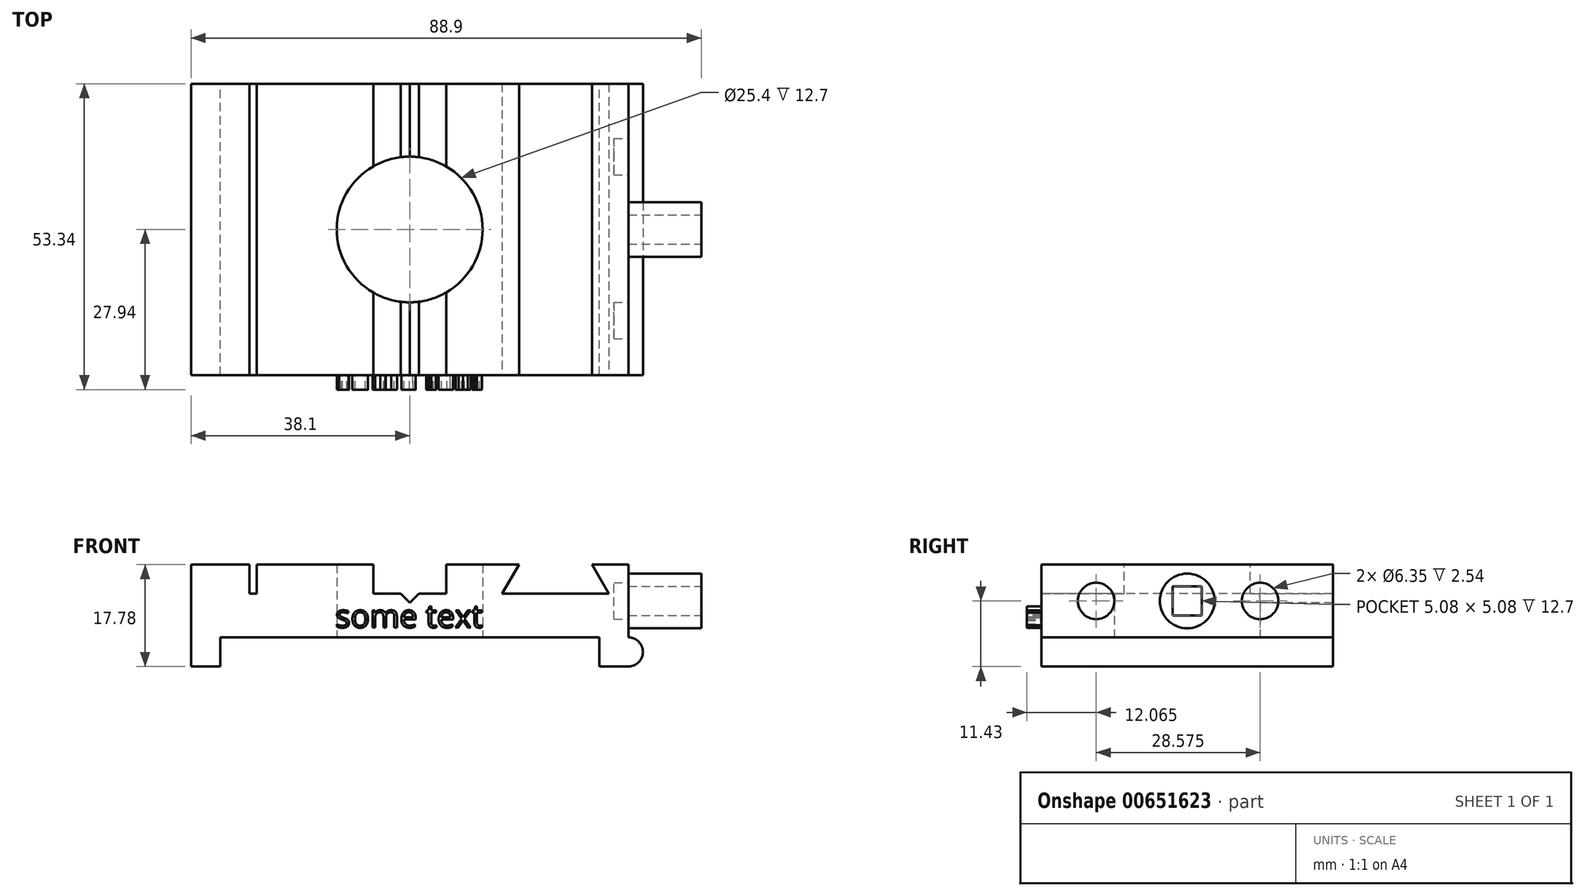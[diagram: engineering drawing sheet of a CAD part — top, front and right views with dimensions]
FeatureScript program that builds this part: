
annotation { "Feature Type Name" : "Feature", "Feature Type Description" : "" }
export const myFeature = defineFeature(function(context is Context, id is Id, definition is map)
    precondition{}
    {
        {
            var Q0;
            Q0=qCreatedBy(makeId("Top.planeOp"),FACE);
            var sketch = newSketch(context, id + "F0", { "sketchPlane" : qUnion([Q0])});
            skLineSegment(sketch, "E0.bottom", {"start": v(38.1, 25.4) * mm, "end": v(-38.1, 25.4) * mm});
            skLineSegment(sketch, "E0.top", {"start": v(38.1, -25.4) * mm, "end": v(-38.1, -25.4) * mm});
            skLineSegment(sketch, "E0.left", {"start": v(38.1, 25.4) * mm, "end": v(38.1, -25.4) * mm});
            skLineSegment(sketch, "E0.right", {"start": v(-38.1, 25.4) * mm, "end": v(-38.1, -25.4) * mm});
            skPoint(sketch, "E0.middle", {"position": v(0, 0) * mm});
            skCircle(sketch, "E1", {"center": v(0, 0) * mm, "radius": 12.7 * mm});
            skSolve(sketch);
        }
        {
            var Q0;
            Q0=makeQuery(id+"F0.imprint","IMPRINT",FACE,{"disambiguationData":[TD([[makeQuery(id+"F0.imprint","IMPRINT",EDGE,{"derivedFrom":sQuery(id+"F0.wireOp",EDGE,"E0.bottom")}),1.0]])]});
            extrude(context, id + "F1", {"entities" : qUnion([Q0]), "depth" : 12.7 * mm});
        }
        {
            var Q0;
            Q0=makeQuery(id+"F1.opExtrude","CAP_FACE",FACE,{"disambiguationData":[OSD([sQuery(id+"F0.wireOp",EDGE,"E0.bottom"),sQuery(id+"F0.wireOp",EDGE,"E0.top"),sQuery(id+"F0.wireOp",EDGE,"E0.left"),sQuery(id+"F0.wireOp",EDGE,"E0.right"),sQuery(id+"F0.wireOp",EDGE,"E1")])],"isStart":false});
            var sketch = newSketch(context, id + "F2", { "sketchPlane" : qUnion([Q0])});
            skLineSegment(sketch, "E2.bottom", {"start": v(-27.94, 25.4) * mm, "end": v(-26.67, 25.4) * mm});
            skLineSegment(sketch, "E2.top", {"start": v(-27.94, -25.4) * mm, "end": v(-26.67, -25.4) * mm});
            skLineSegment(sketch, "E2.left", {"start": v(-27.94, 25.4) * mm, "end": v(-27.94, -25.4) * mm});
            skLineSegment(sketch, "E2.right", {"start": v(-26.67, 25.4) * mm, "end": v(-26.67, -25.4) * mm});
            skLineSegment(sketch, "E3", {"start": v(-6.35, 25.4) * mm, "end": v(-6.35, -25.4) * mm});
            skLineSegment(sketch, "E4", {"start": v(-6.35, -25.4) * mm, "end": v(6.35, -25.4) * mm});
            skLineSegment(sketch, "E5", {"start": v(6.35, -25.4) * mm, "end": v(6.35, 25.4) * mm});
            skLineSegment(sketch, "E6", {"start": v(6.35, 25.4) * mm, "end": v(-6.35, 25.4) * mm});
            skPoint(sketch, "E7", {"position": v(0, 0) * mm});
            skLineSegment(sketch, "E8", {"start": v(0, 25.4) * mm, "end": v(0, -25.4) * mm, "construction": true});
            skSolve(sketch);
        }
        {
            var Q0;
            Q0=makeQuery(id+"F2.imprint","IMPRINT",FACE,{"disambiguationData":[TD([[makeQuery(id+"F2.imprint","IMPRINT",EDGE,{"derivedFrom":sQuery(id+"F2.wireOp",EDGE,"E2.bottom")}),1.0]])]});
            var Q1;
            {var subQ0=sQuery(id+"F2.wireOp",EDGE,"E4");Q1=makeQuery(id+"F2.imprint","IMPRINT",FACE,{"disambiguationData":[TD([[makeQuery(id+"F2.imprint","IMPRINT",EDGE,{"derivedFrom":subQ0}),-1.0]])]});}
            var Q2;
            {var subQ0=sQuery(id+"F2.wireOp",EDGE,"E6");Q2=makeQuery(id+"F2.imprint","IMPRINT",FACE,{"disambiguationData":[TD([[makeQuery(id+"F2.imprint","IMPRINT",EDGE,{"derivedFrom":subQ0}),1.0]])]});}
            extrude(context, id + "F3", {"entities" : qUnion([Q0, Q1, Q2]), "operationType" : NewBodyOperationType.REMOVE, "oppositeDirection" : true, "depth" : 5.08 * mm});
        }
        {
            var Q0;
            Q0=makeQuery(id+"F1.opExtrude","SWEPT_FACE",FACE,{"disambiguationData":[OSD([sQuery(id+"F0.wireOp",EDGE,"E0.top")])]});
            var sketch = newSketch(context, id + "F4", { "sketchPlane" : qUnion([Q0])});
            skLineSegment(sketch, "E9", {"start": v(19.05, 12.7) * mm, "end": v(16.12, 7.62) * mm});
            skLineSegment(sketch, "E10", {"start": v(16.12, 7.62) * mm, "end": v(34.68, 7.62) * mm});
            skLineSegment(sketch, "E11", {"start": v(34.68, 7.62) * mm, "end": v(31.75, 12.7) * mm});
            skLineSegment(sketch, "E12", {"start": v(31.75, 12.7) * mm, "end": v(19.05, 12.7) * mm});
            skLineSegment(sketch, "E13", {"start": v(25.4, 7.62) * mm, "end": v(25.4, 12.7) * mm, "construction": true});
            skSolve(sketch);
        }
        {
            var Q0;
            Q0=makeQuery(id+"F4.imprint","IMPRINT",FACE,{"disambiguationData":[TD([[makeQuery(id+"F4.imprint","IMPRINT",EDGE,{"derivedFrom":sQuery(id+"F4.wireOp",EDGE,"E9")}),1.0]])]});
            extrude(context, id + "F5", {"entities" : qUnion([Q0]), "operationType" : NewBodyOperationType.REMOVE, "endBound" : BoundingType.THROUGH_ALL, "oppositeDirection" : true, "depth" : 25.4 * mm});
        }
        {
            var Q0;
            Q0=makeQuery(id+"F1.opExtrude","SWEPT_FACE",FACE,{"disambiguationData":[OSD([sQuery(id+"F0.wireOp",EDGE,"E0.left")])]});
            var sketch = newSketch(context, id + "F6", { "sketchPlane" : qUnion([Q0])});
            skCircle(sketch, "E14", {"center": v(0, 6.35) * mm, "radius": 4.76 * mm});
            skPoint(sketch, "E14.centerSnap0", {"position": v(-25.4, 6.35) * mm});
            skPoint(sketch, "E14.centerSnap1", {"position": v(0, 12.7) * mm});
            skSolve(sketch);
        }
        {
            var Q0;
            Q0=makeQuery(id+"F6.imprint","IMPRINT",FACE,{"disambiguationData":[TD([[makeQuery(id+"F6.imprint","IMPRINT",EDGE,{"derivedFrom":sQuery(id+"F6.wireOp",EDGE,"E14")}),1.0]])]});
            extrude(context, id + "F7", {"entities" : qUnion([Q0]), "operationType" : NewBodyOperationType.ADD, "depth" : 12.7 * mm});
        }
        {
            var Q0;
            Q0=makeQuery(id+"F1.opExtrude","CAP_FACE",FACE,{"disambiguationData":[OSD([sQuery(id+"F0.wireOp",EDGE,"E0.bottom"),sQuery(id+"F0.wireOp",EDGE,"E0.top"),sQuery(id+"F0.wireOp",EDGE,"E0.left"),sQuery(id+"F0.wireOp",EDGE,"E0.right"),sQuery(id+"F0.wireOp",EDGE,"E1")])],"isStart":true});
            var sketch = newSketch(context, id + "F8", { "sketchPlane" : qUnion([Q0])});
            skLineSegment(sketch, "E15.bottom", {"start": v(-38.1, 25.4) * mm, "end": v(-33.02, 25.4) * mm});
            skLineSegment(sketch, "E15.top", {"start": v(-38.1, -25.4) * mm, "end": v(-33.02, -25.4) * mm});
            skLineSegment(sketch, "E15.left", {"start": v(-38.1, 25.4) * mm, "end": v(-38.1, -25.4) * mm});
            skLineSegment(sketch, "E15.right", {"start": v(-33.02, 25.4) * mm, "end": v(-33.02, -25.4) * mm});
            skLineSegment(sketch, "E16.bottom", {"start": v(38.1, 25.4) * mm, "end": v(33.02, 25.4) * mm});
            skLineSegment(sketch, "E16.top", {"start": v(38.1, -25.4) * mm, "end": v(33.02, -25.4) * mm});
            skLineSegment(sketch, "E16.left", {"start": v(38.1, 25.4) * mm, "end": v(38.1, -25.4) * mm});
            skLineSegment(sketch, "E16.right", {"start": v(33.02, 25.4) * mm, "end": v(33.02, -25.4) * mm});
            skSolve(sketch);
        }
        {
            var Q0;
            Q0=makeQuery(id+"F8.imprint","IMPRINT",FACE,{"disambiguationData":[TD([[makeQuery(id+"F8.imprint","IMPRINT",EDGE,{"derivedFrom":sQuery(id+"F8.wireOp",EDGE,"E15.bottom")}),1.0]])]});
            var Q1;
            Q1=makeQuery(id+"F8.imprint","IMPRINT",FACE,{"disambiguationData":[TD([[makeQuery(id+"F8.imprint","IMPRINT",EDGE,{"derivedFrom":sQuery(id+"F8.wireOp",EDGE,"E16.bottom")}),1.0]])]});
            extrude(context, id + "F9", {"entities" : qUnion([Q0, Q1]), "operationType" : NewBodyOperationType.ADD, "depth" : 5.08 * mm, "offsetDistance" : 25.4 * mm});
        }
        {
            var Q0;
            Q0=makeQuery(id+"F7.opExtrude","CAP_FACE",FACE,{"disambiguationData":[OSD([sQuery(id+"F6.wireOp",EDGE,"E14")])],"isStart":false});
            var sketch = newSketch(context, id + "F10", { "sketchPlane" : qUnion([Q0])});
            skLineSegment(sketch, "E17.bottom", {"start": v(-2.54, 8.9) * mm, "end": v(2.54, 8.9) * mm});
            skLineSegment(sketch, "E17.top", {"start": v(-2.54, 3.81) * mm, "end": v(2.54, 3.81) * mm});
            skLineSegment(sketch, "E17.left", {"start": v(-2.54, 8.9) * mm, "end": v(-2.54, 3.81) * mm});
            skLineSegment(sketch, "E17.right", {"start": v(2.54, 8.9) * mm, "end": v(2.54, 3.81) * mm});
            skPoint(sketch, "E17.middle", {"position": v(0, 6.35) * mm});
            skSolve(sketch);
        }
        {
            var Q0;
            Q0 = qSketchRegion(id + "F10", true);
            extrude(context, id + "F11", {"entities" : qUnion([Q0]), "operationType" : NewBodyOperationType.REMOVE, "oppositeDirection" : true, "depth" : 12.7 * mm, "offsetDistance" : 25.4 * mm});
        }
        {
            var Q0;
            Q0=makeQuery(id+"F9.boolean.opBoolean","MERGE",FACE,{"derivedFrom":[makeQuery(id+"F1.opExtrude","SWEPT_FACE",FACE,{"disambiguationData":[OSD([sQuery(id+"F0.wireOp",EDGE,"E0.top")])]}),makeQuery(id+"F9.opExtrude","SWEPT_FACE",FACE,{"disambiguationData":[OSD([sQuery(id+"F8.wireOp",EDGE,"E15.bottom")])]}),makeQuery(id+"F9.opExtrude","SWEPT_FACE",FACE,{"disambiguationData":[OSD([sQuery(id+"F8.wireOp",EDGE,"E16.bottom")])]})]});
            var sketch = newSketch(context, id + "F12", { "sketchPlane" : qUnion([Q0])});
            skCircle(sketch, "E18", {"center": v(38.1, -2.54) * mm, "radius": 2.54 * mm});
            skLineSegment(sketch, "E19", {"start": v(38.1, 0) * mm, "end": v(38.1, -5.08) * mm});
            skSolve(sketch);
        }
        {
            var Q0;
            {var subQ0=sQuery(id+"F12.wireOp",EDGE,"E19");Q0=makeQuery(id+"F12.imprint","IMPRINT",FACE,{"disambiguationData":[TD([[makeQuery(id+"F12.imprint","IMPRINT",EDGE,{"derivedFrom":subQ0}),1.0]])]});}
            var Q1;
            Q1=makeQuery(id+"F9.boolean.opBoolean","MERGE",FACE,{"derivedFrom":[makeQuery(id+"F1.opExtrude","SWEPT_FACE",FACE,{"disambiguationData":[OSD([sQuery(id+"F0.wireOp",EDGE,"E0.bottom")])]}),makeQuery(id+"F9.opExtrude","SWEPT_FACE",FACE,{"disambiguationData":[OSD([sQuery(id+"F8.wireOp",EDGE,"E15.top")])]}),makeQuery(id+"F9.opExtrude","SWEPT_FACE",FACE,{"disambiguationData":[OSD([sQuery(id+"F8.wireOp",EDGE,"E16.top")])]})]});
            extrude(context, id + "F13", {"entities" : qUnion([Q0]), "operationType" : NewBodyOperationType.ADD, "endBound" : BoundingType.UP_TO_SURFACE, "oppositeDirection" : true, "depth" : 25.4 * mm, "endBoundEntityFace" : qUnion([Q1]), "offsetDistance" : 25.4 * mm});
        }
        {
            var Q0;
            Q0=makeQuery(id+"F9.boolean.opBoolean","MERGE",FACE,{"derivedFrom":[makeQuery(id+"F1.opExtrude","SWEPT_FACE",FACE,{"disambiguationData":[OSD([sQuery(id+"F0.wireOp",EDGE,"E0.left")])]}),makeQuery(id+"F9.opExtrude","SWEPT_FACE",FACE,{"disambiguationData":[OSD([sQuery(id+"F8.wireOp",EDGE,"E16.left")])]})]});
            var sketch = newSketch(context, id + "F14", { "sketchPlane" : qUnion([Q0])});
            skCircle(sketch, "E20.0", {"center": v(0, 6.35) * mm, "radius": 4.76 * mm});
            skLineSegment(sketch, "E21", {"start": v(-25.4, 6.35) * mm, "end": v(25.4, 6.35) * mm, "construction": true});
            skCircle(sketch, "E22", {"center": v(-15.87, 6.35) * mm, "radius": 3.18 * mm});
            skCircle(sketch, "E23", {"center": v(12.7, 6.35) * mm, "radius": 3.18 * mm});
            skSolve(sketch);
        }
        {
            var Q0;
            Q0=makeQuery(id+"F14.imprint","IMPRINT",FACE,{"disambiguationData":[TD([[makeQuery(id+"F14.imprint","IMPRINT",EDGE,{"derivedFrom":sQuery(id+"F14.wireOp",EDGE,"E20.0")}),-1.0]])]});
            var sketch = newSketch(context, id + "F15", { "sketchPlane" : qUnion([Q0])});
            skSolve(sketch);
        }
        {
            var Q0;
            Q0=makeQuery(id+"F15.imprint","IMPRINT",FACE,{"disambiguationData":[TD([[makeQuery(id+"F15.imprint","IMPRINT",EDGE,{"derivedFrom":makeQuery(id+"F14.imprint","IMPRINT",EDGE,{"derivedFrom":sQuery(id+"F14.wireOp",EDGE,"E22")})}),1.0]])]});
            var Q1;
            Q1=makeQuery(id+"F15.imprint","IMPRINT",FACE,{"disambiguationData":[TD([[makeQuery(id+"F15.imprint","IMPRINT",EDGE,{"derivedFrom":makeQuery(id+"F14.imprint","IMPRINT",EDGE,{"derivedFrom":sQuery(id+"F14.wireOp",EDGE,"E23")})}),1.0]])]});
            var Q2;
            Q2=sQuery(id+"F14.wireOp",EDGE,"E22");
            var Q3;
            Q3=sQuery(id+"F14.wireOp",EDGE,"E23");
            extrude(context, id + "F16", {"entities" : qUnion([Q0, Q1]), "operationType" : NewBodyOperationType.REMOVE, "surfaceEntities" : qUnion([Q2, Q3]), "oppositeDirection" : true, "depth" : 2.54 * mm, "offsetDistance" : 25.4 * mm});
        }
        {
            var Q0;
            {var subQ0=sQuery(id+"F12.wireOp",EDGE,"E19");var subQ1=sQuery(id+"F12.wireOp",EDGE,"E18");Q0=makeQuery(id+"F4gUPaBvnwU2ioe_1.1.F13.boolean.opBoolean","MERGE",FACE,{"derivedFrom":[makeQuery(id+"F13.boolean.opBoolean","MERGE",FACE,{"derivedFrom":[makeQuery(id+"F9.boolean.opBoolean","MERGE",FACE,{"derivedFrom":[makeQuery(id+"F1.opExtrude","SWEPT_FACE",FACE,{"disambiguationData":[OSD([sQuery(id+"F0.wireOp",EDGE,"E0.top")])]}),makeQuery(id+"F9.opExtrude","SWEPT_FACE",FACE,{"disambiguationData":[OSD([sQuery(id+"F8.wireOp",EDGE,"E15.bottom")])]}),makeQuery(id+"F9.opExtrude","SWEPT_FACE",FACE,{"disambiguationData":[OSD([sQuery(id+"F8.wireOp",EDGE,"E16.bottom")])]})]}),makeQuery(id+"F13.opExtrude","CAP_FACE",FACE,{"disambiguationData":[OSD([subQ1,subQ0])],"isStart":true})]}),makeQuery(id+"F4gUPaBvnwU2ioe_1.1.F13.opExtrude","CAP_FACE",FACE,{"disambiguationData":[OSD([subQ1,subQ0])],"isStart":true})]});}
            var sketch = newSketch(context, id + "F17", { "sketchPlane" : qUnion([Q0])});
            skLineSegment(sketch, "E24", {"start": v(-1.59, 7.62) * mm, "end": v(0, 6.03) * mm});
            skLineSegment(sketch, "E25", {"start": v(0, 6.03) * mm, "end": v(1.59, 7.62) * mm});
            skLineSegment(sketch, "E26", {"start": v(1.59, 7.62) * mm, "end": v(-1.59, 7.62) * mm});
            skSolve(sketch);
        }
        {
            var Q0;
            Q0=makeQuery(id+"F17.imprint","IMPRINT",FACE,{"disambiguationData":[TD([[makeQuery(id+"F17.imprint","IMPRINT",EDGE,{"derivedFrom":sQuery(id+"F17.wireOp",EDGE,"E24")}),1.0]])]});
            extrude(context, id + "F18", {"entities" : qUnion([Q0]), "operationType" : NewBodyOperationType.REMOVE, "endBound" : BoundingType.THROUGH_ALL, "oppositeDirection" : true, "depth" : 25.4 * mm, "offsetDistance" : 25.4 * mm});
        }
        {
            var Q0;
            {var subQ0=sQuery(id+"F12.wireOp",EDGE,"E19");var subQ1=sQuery(id+"F12.wireOp",EDGE,"E18");Q0=makeQuery(id+"F4gUPaBvnwU2ioe_1.1.F13.boolean.opBoolean","MERGE",FACE,{"derivedFrom":[makeQuery(id+"F13.boolean.opBoolean","MERGE",FACE,{"derivedFrom":[makeQuery(id+"F9.boolean.opBoolean","MERGE",FACE,{"derivedFrom":[makeQuery(id+"F1.opExtrude","SWEPT_FACE",FACE,{"disambiguationData":[OSD([sQuery(id+"F0.wireOp",EDGE,"E0.top")])]}),makeQuery(id+"F9.opExtrude","SWEPT_FACE",FACE,{"disambiguationData":[OSD([sQuery(id+"F8.wireOp",EDGE,"E15.bottom")])]}),makeQuery(id+"F9.opExtrude","SWEPT_FACE",FACE,{"disambiguationData":[OSD([sQuery(id+"F8.wireOp",EDGE,"E16.bottom")])]})]}),makeQuery(id+"F13.opExtrude","CAP_FACE",FACE,{"disambiguationData":[OSD([subQ1,subQ0])],"isStart":true})]}),makeQuery(id+"F4gUPaBvnwU2ioe_1.1.F13.opExtrude","CAP_FACE",FACE,{"disambiguationData":[OSD([subQ1,subQ0])],"isStart":true})]});}
            var sketch = newSketch(context, id + "F19", { "sketchPlane" : qUnion([Q0])});
            skText(sketch, "E27", { "text": "some text", "fontName": "OpenSans-Regular.ttf"});
            skLineSegment(sketch, "E28", {"start": v(0, 0) * mm, "end": v(0, 6.03) * mm, "construction": true});
            const initialGuessF19  = {"E27": [-0.01295, 0.00172, 1, 0, 0.004]};
            skSetInitialGuess(sketch, initialGuessF19);
            skSolve(sketch);
        }
        {
            var Q0;
            Q0 = qSketchRegion(id + "F19", true);
            extrude(context, id + "F20", {"entities" : qUnion([Q0]), "operationType" : NewBodyOperationType.ADD, "depth" : 2.54 * mm, "offsetDistance" : 25.4 * mm});
        }
    });
